# Revit family: Valve_Trim-DXV-Equility-D35109510_Series
name_source: partatom
category: Plumbing Fixtures
revit_build: Autodesk Revit 2014 (Build: 20130308_1515(x64)
units: mm (PartAtom-declared; Revit-internal decimal feet)

## types (6) — shared parameters
Assembly Code = D2010710
CW Connection = Yes
CWFU = 3
Cold Water Connection Diameter = 1/2"
Cold Water Connection Radius = 1/4"
Default Elevation = 40"
Description = Equility Pressure Balance Tub/Shower Valve Trim With Diverter
HW Connection = Yes
HWFU = 3
Height = 8 3/8"
Hot Water Connection Diameter = 1"
Hot Water Connection Radius = 1/4"
Installation Type = Wall Mounted
Length = 3 3/16"
Manufacturer = DXV
Price = Prices may vary. Please consult Manufacturer Representative for most up-to-date price list.
Product Documentation Link = https://dxv01.blob.core.windows.net
Product Page URL = https://www.dxv.com
Revised Date = 12/18/2018
Shower Rough Location = 1 5/8"
Tempered Water Connection = Yes
Tempered Water Connection Diameter = 1/2"
Tempered Water Connection Radius = 1/4"
URL = http://www.dxv.com
Vent Connection = No
WFU = 4
Warranty Documentation Link = https://www.dxv.com
Waste Connection = Yes
Width = 6 11/16"

## per-type parameters (varying)
| type | Finish | Material |
| D35109510.100 | Cast Brass-DXV-100-Polished Chrome | Cast Brass-DXV-100-Polished Chrome |
| D35109510.144 | Cast Brass-DXV-144-Brushed Nickel | Cast Brass-DXV-144-Brushed Nickel |
| D35109510.243 | Cast Brass-DXV-243-Matte Black | Cast Brass-DXV-243-Matte Black |
| D35109510RB.100 | Cast Brass-DXV-100-Polished Chrome | Cast Brass-DXV-100-Polished Chrome |
| D35109510RB.144 | Cast Brass-DXV-144-Brushed Nickel | Cast Brass-DXV-144-Brushed Nickel |
| D35109510RB.243 | Cast Brass-DXV-243-Matte Black | Cast Brass-DXV-243-Matte Black |

note: column(s) folded — value = type name in every type: Model

## geometry (parser evidence)
native form markers: Sweep x3
no freeform markers — native parametric forms only
